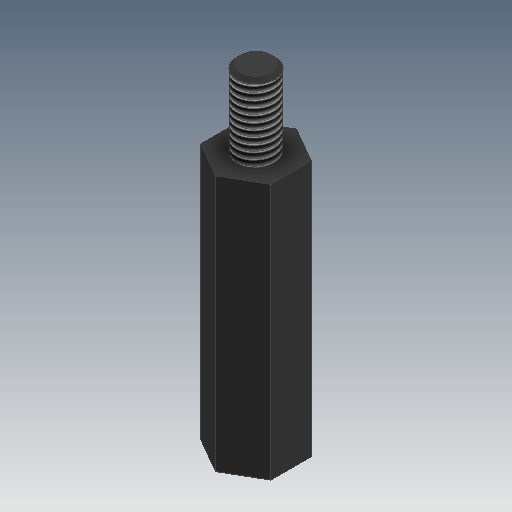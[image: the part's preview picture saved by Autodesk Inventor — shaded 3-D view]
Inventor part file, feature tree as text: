
AUTODESK INVENTOR PART (.ipt)
format: ipt  version: 2020 (Build 240168000, 168)  size: 124,416 bytes
history: native  units: in
note: dims shown in document units (in); Inventor stores cm internally (conversion verified against a paired STEP export)
features: extrude x3, sketch x3, thread x2, chamfer x2
ambient origin geometry x8: Origin, YZ Plane, XZ Plane, XY Plane, X Axis, Y Axis, Z Axis, Center Point
bodies: Solid1 (feature_tree)
feature tree (10):
  extrude  "Extrusion1"  Depth=0.7874in TaperAngle=0.0deg
  extrude  "Extrusion2"  Depth=0.2362in TaperAngle=0.0deg
  thread  "Thread1"  [1 undecoded]
  chamfer  "Chamfer1"  Distance=0.0118in Angle=45.0deg
  extrude  "Extrusion3"  Depth=0.2756in TaperAngle=0.0deg
  thread  "Thread2"  [1 undecoded]
  chamfer  "Chamfer2"  Distance=0.0118in Angle=45.0deg
  sketch  "Sketch1"  dims[d0=0.2157in d1=0.7874in d2=0.0in]
  sketch  "Sketch2"  dims[d3=0.1181in d4=0.2362in d5=0.0in d6=0.2362in d7=0.0in d8=0.0118in d9=0.0787in d10=45.0deg]
  sketch  "Sketch3"  dims[d11=0.1181in d12=0.2756in d13=0.0in d14=0.2756in d15=0.0in d16=0.0118in d17=0.0787in d18=45.0deg]
note: 2 required parameter values undecoded (feature->parameter linkage not recoverable at this tier; creation-order binding heuristic only, values carry confidence <= 0.55)
